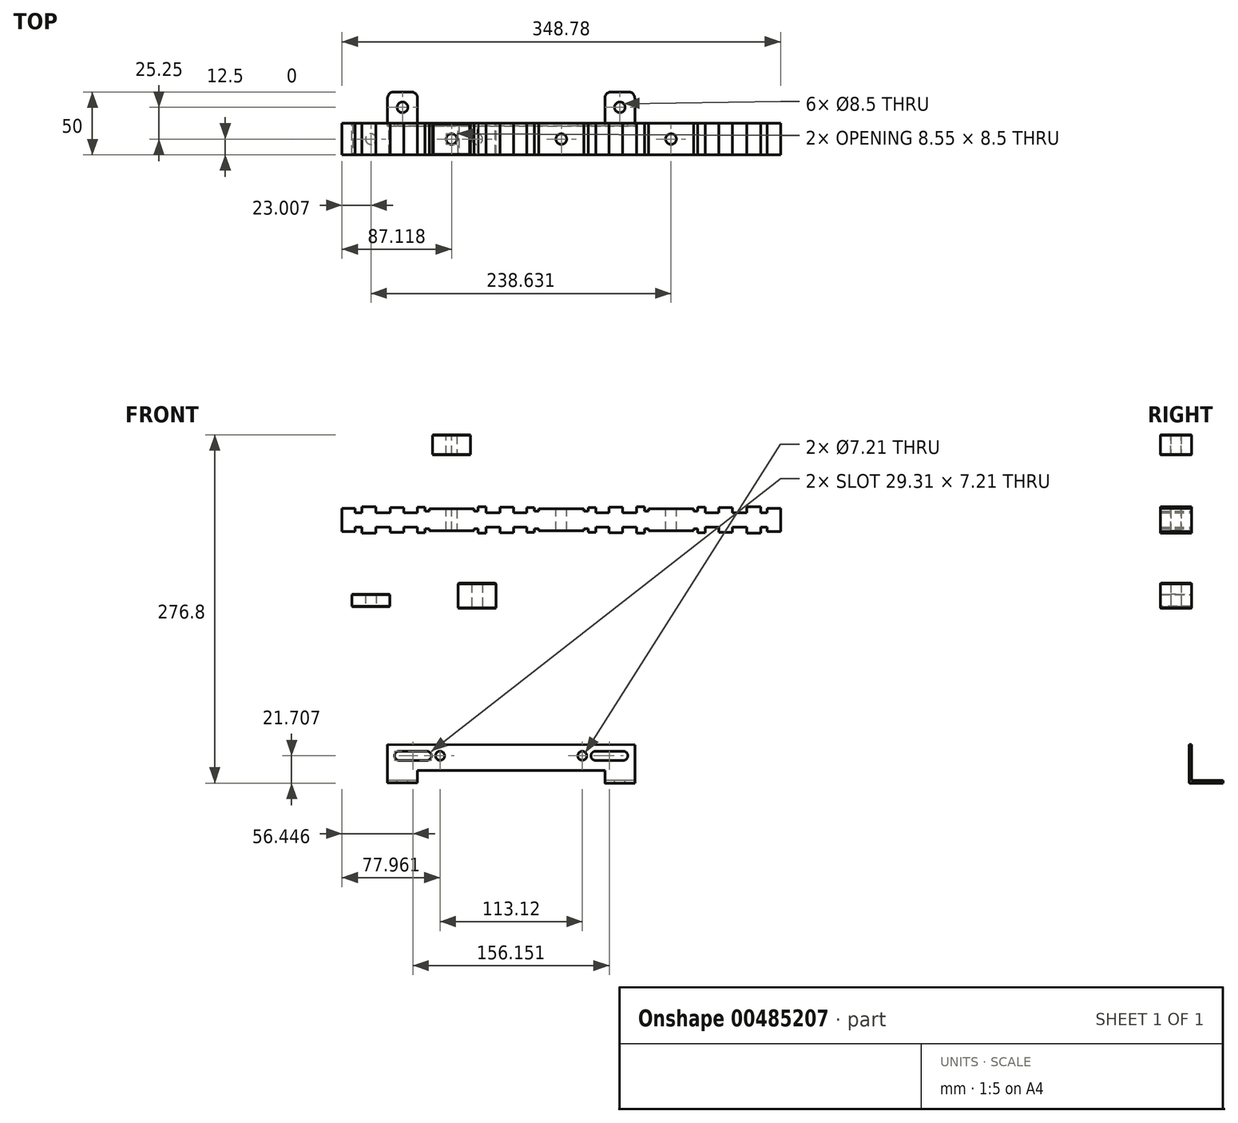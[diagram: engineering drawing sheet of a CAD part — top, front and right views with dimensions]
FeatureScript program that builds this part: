
annotation { "Feature Type Name" : "Feature", "Feature Type Description" : "" }
export const myFeature = defineFeature(function(context is Context, id is Id, definition is map)
    precondition{}
    {
        {
            var Q0;
            Q0=qCreatedBy(makeId("Front.planeOp"),FACE);
            var sketch = newSketch(context, id + "F0", { "sketchPlane" : qUnion([Q0])});
            skLineSegment(sketch, "E0", {"start": v(-156.91, 5.74) * mm, "end": v(-156.91, -3.35) * mm});
            skLineSegment(sketch, "E1", {"start": v(-156.91, -3.35) * mm, "end": v(-146.35, -3.35) * mm});
            skLineSegment(sketch, "E2", {"start": v(-146.35, -3.35) * mm, "end": v(-146.35, 0) * mm});
            skLineSegment(sketch, "E3", {"start": v(-146.35, 0) * mm, "end": v(-141.22, 0) * mm});
            skLineSegment(sketch, "E4", {"start": v(-141.22, 0) * mm, "end": v(-141.22, -4.82) * mm});
            skLineSegment(sketch, "E5", {"start": v(-141.22, -4.82) * mm, "end": v(-129.92, -4.82) * mm});
            skLineSegment(sketch, "E6", {"start": v(-129.92, -4.82) * mm, "end": v(-129.92, 0) * mm});
            skLineSegment(sketch, "E7", {"start": v(-129.92, 0) * mm, "end": v(-118.63, 0) * mm});
            skLineSegment(sketch, "E8", {"start": v(-118.63, 0) * mm, "end": v(-118.63, -4.17) * mm});
            skLineSegment(sketch, "E9", {"start": v(-118.63, -4.17) * mm, "end": v(-107.86, -4.17) * mm});
            skLineSegment(sketch, "E10", {"start": v(-107.86, -4.17) * mm, "end": v(-107.86, 0) * mm});
            skLineSegment(sketch, "E11", {"start": v(-107.86, 0) * mm, "end": v(-96.96, 0) * mm});
            skLineSegment(sketch, "E12", {"start": v(-96.96, 0) * mm, "end": v(-96.96, -4.43) * mm});
            skLineSegment(sketch, "E13", {"start": v(-96.96, -4.43) * mm, "end": v(-90.86, -4.43) * mm});
            skLineSegment(sketch, "E14", {"start": v(-90.86, -4.43) * mm, "end": v(-90.86, -1.18) * mm});
            skLineSegment(sketch, "E15", {"start": v(-90.86, -1.18) * mm, "end": v(-87.61, -1.18) * mm});
            skLineSegment(sketch, "E16", {"start": v(-87.61, -1.18) * mm, "end": v(-87.61, -3) * mm});
            skLineSegment(sketch, "E17", {"start": v(-87.61, -3) * mm, "end": v(-51.92, -3) * mm});
            skLineSegment(sketch, "E18", {"start": v(-51.92, -3) * mm, "end": v(-51.92, -1.18) * mm});
            skPoint(sketch, "E18.endSnap0", {"position": v(-89.24, -1.18) * mm});
            skLineSegment(sketch, "E19", {"start": v(-51.92, -1.18) * mm, "end": v(-48.79, -1.18) * mm});
            skLineSegment(sketch, "E20", {"start": v(-48.79, -1.18) * mm, "end": v(-48.79, -4.73) * mm});
            skLineSegment(sketch, "E21", {"start": v(-48.79, -4.73) * mm, "end": v(-42.49, -4.73) * mm});
            skLineSegment(sketch, "E22", {"start": v(-42.49, -4.73) * mm, "end": v(-42.49, 0) * mm});
            skLineSegment(sketch, "E23", {"start": v(-42.49, 0) * mm, "end": v(-31.4, 0) * mm});
            skLineSegment(sketch, "E24", {"start": v(-31.4, 0) * mm, "end": v(-31.4, -4.37) * mm});
            skLineSegment(sketch, "E25", {"start": v(-31.4, -4.37) * mm, "end": v(-20.51, -4.37) * mm});
            skLineSegment(sketch, "E26", {"start": v(-20.51, -4.37) * mm, "end": v(-20.51, 0) * mm});
            skLineSegment(sketch, "E27", {"start": v(-20.51, 0) * mm, "end": v(-9.94, 0) * mm});
            skLineSegment(sketch, "E28", {"start": v(-9.94, 0) * mm, "end": v(-9.94, -4.17) * mm});
            skLineSegment(sketch, "E29", {"start": v(-9.94, -4.17) * mm, "end": v(-4.1, -4.17) * mm});
            skLineSegment(sketch, "E30", {"start": v(-4.1, -4.17) * mm, "end": v(-4.1, -1.18) * mm});
            skLineSegment(sketch, "E31", {"start": v(-4.1, -1.18) * mm, "end": v(-0.58, -1.18) * mm});
            skLineSegment(sketch, "E32", {"start": v(-0.58, -1.18) * mm, "end": v(-0.58, -3) * mm});
            skLineSegment(sketch, "E33", {"start": v(-0.58, -3) * mm, "end": v(17.48, -3) * mm});
            skLineSegment(sketch, "E34.MirrorCS", {"start": v(-4.1, 15.64) * mm, "end": v(-4.1, 12.65) * mm});
            skLineSegment(sketch, "E35.MirrorCS", {"start": v(-90.86, 15.9) * mm, "end": v(-90.86, 12.65) * mm});
            skLineSegment(sketch, "E36.MirrorCS", {"start": v(-90.86, 12.65) * mm, "end": v(-87.61, 12.65) * mm});
            skLineSegment(sketch, "E37.MirrorCS", {"start": v(-4.1, 12.65) * mm, "end": v(-0.58, 12.65) * mm});
            skLineSegment(sketch, "E38.MirrorCS", {"start": v(-96.96, 11.47) * mm, "end": v(-96.96, 15.9) * mm});
            skLineSegment(sketch, "E39.MirrorCS", {"start": v(-9.94, 15.64) * mm, "end": v(-4.1, 15.64) * mm});
            skLineSegment(sketch, "E40.MirrorCS", {"start": v(-96.96, 15.9) * mm, "end": v(-90.86, 15.9) * mm});
            skLineSegment(sketch, "E41.MirrorCS", {"start": v(-87.61, 12.65) * mm, "end": v(-87.61, 14.47) * mm});
            skLineSegment(sketch, "E42.MirrorCS", {"start": v(-0.58, 12.65) * mm, "end": v(-0.58, 14.47) * mm});
            skLineSegment(sketch, "E43.MirrorCS", {"start": v(-20.51, 15.84) * mm, "end": v(-20.51, 11.47) * mm});
            skLineSegment(sketch, "E44.MirrorCS", {"start": v(-107.86, 15.64) * mm, "end": v(-107.86, 11.47) * mm});
            skLineSegment(sketch, "E45.MirrorCS", {"start": v(-146.35, 11.47) * mm, "end": v(-141.22, 11.47) * mm});
            skLineSegment(sketch, "E46.MirrorCS", {"start": v(-156.91, 14.82) * mm, "end": v(-146.35, 14.82) * mm});
            skLineSegment(sketch, "E47.MirrorCS", {"start": v(-146.35, 14.82) * mm, "end": v(-146.35, 11.47) * mm});
            skLineSegment(sketch, "E48.MirrorCS", {"start": v(-141.22, 11.47) * mm, "end": v(-141.22, 16.29) * mm});
            skLineSegment(sketch, "E49.MirrorCS", {"start": v(-156.91, 5.74) * mm, "end": v(-156.91, 14.82) * mm});
            skLineSegment(sketch, "E50.MirrorCS", {"start": v(-51.92, 12.65) * mm, "end": v(-48.79, 12.65) * mm});
            skLineSegment(sketch, "E51.MirrorCS", {"start": v(-42.49, 11.47) * mm, "end": v(-31.4, 11.47) * mm});
            skLineSegment(sketch, "E52.MirrorCS", {"start": v(-51.92, 14.47) * mm, "end": v(-51.92, 12.65) * mm});
            skLineSegment(sketch, "E53.MirrorCS", {"start": v(-9.94, 11.47) * mm, "end": v(-9.94, 15.64) * mm});
            skLineSegment(sketch, "E54.MirrorCS", {"start": v(-48.79, 16.2) * mm, "end": v(-42.49, 16.2) * mm});
            skLineSegment(sketch, "E55.MirrorCS", {"start": v(-107.86, 11.47) * mm, "end": v(-96.96, 11.47) * mm});
            skLineSegment(sketch, "E56.MirrorCS", {"start": v(-118.63, 11.47) * mm, "end": v(-118.63, 15.64) * mm});
            skLineSegment(sketch, "E57.MirrorCS", {"start": v(-31.4, 11.47) * mm, "end": v(-31.4, 15.84) * mm});
            skLineSegment(sketch, "E58.MirrorCS", {"start": v(-31.4, 15.84) * mm, "end": v(-20.51, 15.84) * mm});
            skLineSegment(sketch, "E59.MirrorCS", {"start": v(-129.92, 16.29) * mm, "end": v(-129.92, 11.47) * mm});
            skLineSegment(sketch, "E60.MirrorCS", {"start": v(-129.92, 11.47) * mm, "end": v(-118.63, 11.47) * mm});
            skLineSegment(sketch, "E61.MirrorCS", {"start": v(-118.63, 15.64) * mm, "end": v(-107.86, 15.64) * mm});
            skLineSegment(sketch, "E62.MirrorCS", {"start": v(-42.49, 16.2) * mm, "end": v(-42.49, 11.47) * mm});
            skLineSegment(sketch, "E63.MirrorCS", {"start": v(-20.51, 11.47) * mm, "end": v(-9.94, 11.47) * mm});
            skLineSegment(sketch, "E64.MirrorCS", {"start": v(-48.79, 12.65) * mm, "end": v(-48.79, 16.2) * mm});
            skLineSegment(sketch, "E65.MirrorCS", {"start": v(-141.22, 16.29) * mm, "end": v(-129.92, 16.29) * mm});
            skLineSegment(sketch, "E66.MirrorCS", {"start": v(-87.61, 14.47) * mm, "end": v(-51.92, 14.47) * mm});
            skLineSegment(sketch, "E67.MirrorCS", {"start": v(-0.58, 14.47) * mm, "end": v(17.48, 14.47) * mm});
            skLineSegment(sketch, "E68.MirrorCS", {"start": v(-84.53, -3.04) * mm, "end": v(-54.8, -3.04) * mm});
            skPoint(sketch, "E69.MirrorP", {"position": v(-89.24, 12.65) * mm});
            skLineSegment(sketch, "E70.MirrorCS", {"start": v(39.06, -1.18) * mm, "end": v(35.54, -1.18) * mm});
            skLineSegment(sketch, "E71.MirrorCS", {"start": v(35.54, -1.18) * mm, "end": v(35.54, -3) * mm});
            skLineSegment(sketch, "E72.MirrorCS", {"start": v(39.06, -4.17) * mm, "end": v(39.06, -1.18) * mm});
            skLineSegment(sketch, "E73.MirrorCS", {"start": v(125.82, -1.18) * mm, "end": v(122.57, -1.18) * mm});
            skLineSegment(sketch, "E74.MirrorCS", {"start": v(125.82, 12.65) * mm, "end": v(122.57, 12.65) * mm});
            skLineSegment(sketch, "E75.MirrorCS", {"start": v(122.57, -1.18) * mm, "end": v(122.57, -3) * mm});
            skLineSegment(sketch, "E76.MirrorCS", {"start": v(83.75, -1.18) * mm, "end": v(83.75, -4.73) * mm});
            skLineSegment(sketch, "E77.MirrorCS", {"start": v(125.82, 15.9) * mm, "end": v(125.82, 12.65) * mm});
            skLineSegment(sketch, "E78.MirrorCS", {"start": v(125.82, -4.43) * mm, "end": v(125.82, -1.18) * mm});
            skLineSegment(sketch, "E79.MirrorCS", {"start": v(86.88, 12.65) * mm, "end": v(83.75, 12.65) * mm});
            skLineSegment(sketch, "E80.MirrorCS", {"start": v(122.57, 12.65) * mm, "end": v(122.57, 14.47) * mm});
            skLineSegment(sketch, "E81.MirrorCS", {"start": v(86.88, -1.18) * mm, "end": v(83.75, -1.18) * mm});
            skLineSegment(sketch, "E82.MirrorCS", {"start": v(86.88, -3) * mm, "end": v(86.88, -1.18) * mm});
            skLineSegment(sketch, "E83.MirrorCS", {"start": v(142.82, 0) * mm, "end": v(131.92, 0) * mm});
            skLineSegment(sketch, "E84.MirrorCS", {"start": v(35.54, 12.65) * mm, "end": v(35.54, 14.47) * mm});
            skLineSegment(sketch, "E85.MirrorCS", {"start": v(55.47, 0) * mm, "end": v(44.9, 0) * mm});
            skLineSegment(sketch, "E86.MirrorCS", {"start": v(164.88, -4.82) * mm, "end": v(164.88, 0) * mm});
            skLineSegment(sketch, "E87.MirrorCS", {"start": v(39.06, 15.64) * mm, "end": v(39.06, 12.65) * mm});
            skLineSegment(sketch, "E88.MirrorCS", {"start": v(77.45, 16.2) * mm, "end": v(77.45, 11.47) * mm});
            skLineSegment(sketch, "E89.MirrorCS", {"start": v(86.88, 14.47) * mm, "end": v(86.88, 12.65) * mm});
            skLineSegment(sketch, "E90.MirrorCS", {"start": v(55.47, 15.84) * mm, "end": v(55.47, 11.47) * mm});
            skLineSegment(sketch, "E91.MirrorCS", {"start": v(83.75, -4.73) * mm, "end": v(77.45, -4.73) * mm});
            skLineSegment(sketch, "E92.MirrorCS", {"start": v(44.9, 0) * mm, "end": v(44.9, -4.17) * mm});
            skLineSegment(sketch, "E93.MirrorCS", {"start": v(153.6, 0) * mm, "end": v(153.6, -4.17) * mm});
            skLineSegment(sketch, "E94.MirrorCS", {"start": v(77.45, 11.47) * mm, "end": v(66.35, 11.47) * mm});
            skLineSegment(sketch, "E95.MirrorCS", {"start": v(181.3, 14.82) * mm, "end": v(181.3, 11.47) * mm});
            skLineSegment(sketch, "E96.MirrorCS", {"start": v(131.92, -4.43) * mm, "end": v(125.82, -4.43) * mm});
            skLineSegment(sketch, "E97.MirrorCS", {"start": v(55.47, 11.47) * mm, "end": v(44.9, 11.47) * mm});
            skLineSegment(sketch, "E98.MirrorCS", {"start": v(44.9, 11.47) * mm, "end": v(44.9, 15.64) * mm});
            skLineSegment(sketch, "E99.MirrorCS", {"start": v(164.88, 11.47) * mm, "end": v(153.6, 11.47) * mm});
            skLineSegment(sketch, "E100.MirrorCS", {"start": v(77.45, -4.73) * mm, "end": v(77.45, 0) * mm});
            skLineSegment(sketch, "E101.MirrorCS", {"start": v(142.82, 15.64) * mm, "end": v(142.82, 11.47) * mm});
            skLineSegment(sketch, "E102.MirrorCS", {"start": v(39.06, 12.65) * mm, "end": v(35.54, 12.65) * mm});
            skLineSegment(sketch, "E103.MirrorCS", {"start": v(44.9, -4.17) * mm, "end": v(39.06, -4.17) * mm});
            skLineSegment(sketch, "E104.MirrorCS", {"start": v(153.6, 11.47) * mm, "end": v(153.6, 15.64) * mm});
            skLineSegment(sketch, "E105.MirrorCS", {"start": v(131.92, 15.9) * mm, "end": v(125.82, 15.9) * mm});
            skLineSegment(sketch, "E106.MirrorCS", {"start": v(131.92, 0) * mm, "end": v(131.92, -4.43) * mm});
            skLineSegment(sketch, "E107.MirrorCS", {"start": v(66.35, 0) * mm, "end": v(66.35, -4.37) * mm});
            skLineSegment(sketch, "E108.MirrorCS", {"start": v(44.9, 15.64) * mm, "end": v(39.06, 15.64) * mm});
            skLineSegment(sketch, "E109.MirrorCS", {"start": v(164.88, 0) * mm, "end": v(153.6, 0) * mm});
            skLineSegment(sketch, "E110.MirrorCS", {"start": v(164.88, 16.29) * mm, "end": v(164.88, 11.47) * mm});
            skLineSegment(sketch, "E111.MirrorCS", {"start": v(191.87, 5.74) * mm, "end": v(191.87, 14.82) * mm});
            skLineSegment(sketch, "E112.MirrorCS", {"start": v(176.17, 0) * mm, "end": v(176.17, -4.82) * mm});
            skLineSegment(sketch, "E113.MirrorCS", {"start": v(142.82, 11.47) * mm, "end": v(131.92, 11.47) * mm});
            skLineSegment(sketch, "E114.MirrorCS", {"start": v(55.47, -4.37) * mm, "end": v(55.47, 0) * mm});
            skLineSegment(sketch, "E115.MirrorCS", {"start": v(131.92, 11.47) * mm, "end": v(131.92, 15.9) * mm});
            skLineSegment(sketch, "E116.MirrorCS", {"start": v(66.35, 11.47) * mm, "end": v(66.35, 15.84) * mm});
            skLineSegment(sketch, "E117.MirrorCS", {"start": v(181.3, 0) * mm, "end": v(176.17, 0) * mm});
            skLineSegment(sketch, "E118.MirrorCS", {"start": v(142.82, -4.17) * mm, "end": v(142.82, 0) * mm});
            skLineSegment(sketch, "E119.MirrorCS", {"start": v(181.3, -3.35) * mm, "end": v(181.3, 0) * mm});
            skLineSegment(sketch, "E120.MirrorCS", {"start": v(181.3, 11.47) * mm, "end": v(176.17, 11.47) * mm});
            skLineSegment(sketch, "E121.MirrorCS", {"start": v(191.87, 5.74) * mm, "end": v(191.87, -3.35) * mm});
            skLineSegment(sketch, "E122.MirrorCS", {"start": v(176.17, 11.47) * mm, "end": v(176.17, 16.29) * mm});
            skLineSegment(sketch, "E123.MirrorCS", {"start": v(83.75, 16.2) * mm, "end": v(77.45, 16.2) * mm});
            skLineSegment(sketch, "E124.MirrorCS", {"start": v(77.45, 0) * mm, "end": v(66.35, 0) * mm});
            skLineSegment(sketch, "E125.MirrorCS", {"start": v(83.75, 12.65) * mm, "end": v(83.75, 16.2) * mm});
            skLineSegment(sketch, "E126.MirrorCS", {"start": v(119.49, -3.04) * mm, "end": v(89.76, -3.04) * mm});
            skLineSegment(sketch, "E127.MirrorCS", {"start": v(122.57, 14.47) * mm, "end": v(86.88, 14.47) * mm});
            skLineSegment(sketch, "E128.MirrorCS", {"start": v(176.17, 16.29) * mm, "end": v(164.88, 16.29) * mm});
            skLineSegment(sketch, "E129.MirrorCS", {"start": v(66.35, 15.84) * mm, "end": v(55.47, 15.84) * mm});
            skPoint(sketch, "E130.MirrorP", {"position": v(124.2, 12.65) * mm});
            skLineSegment(sketch, "E131.MirrorCS", {"start": v(119.49, 14.51) * mm, "end": v(89.76, 14.51) * mm});
            skPoint(sketch, "E132.MirrorP", {"position": v(124.2, -1.18) * mm});
            skLineSegment(sketch, "E133.MirrorCS", {"start": v(153.6, -4.17) * mm, "end": v(142.82, -4.17) * mm});
            skLineSegment(sketch, "E134.MirrorCS", {"start": v(35.54, 14.47) * mm, "end": v(17.48, 14.47) * mm});
            skLineSegment(sketch, "E135.MirrorCS", {"start": v(66.35, -4.37) * mm, "end": v(55.47, -4.37) * mm});
            skLineSegment(sketch, "E136.MirrorCS", {"start": v(176.17, -4.82) * mm, "end": v(164.88, -4.82) * mm});
            skLineSegment(sketch, "E137.MirrorCS", {"start": v(153.6, 15.64) * mm, "end": v(142.82, 15.64) * mm});
            skLineSegment(sketch, "E138.MirrorCS", {"start": v(35.54, -3) * mm, "end": v(17.48, -3) * mm});
            skLineSegment(sketch, "E139.MirrorCS", {"start": v(191.87, 14.82) * mm, "end": v(181.3, 14.82) * mm});
            skLineSegment(sketch, "E140.MirrorCS", {"start": v(122.57, -3) * mm, "end": v(86.88, -3) * mm});
            skLineSegment(sketch, "E141.MirrorCS", {"start": v(191.87, -3.35) * mm, "end": v(181.3, -3.35) * mm});
            skSolve(sketch);
        }
        {
            var Q0;
            Q0=makeQuery(id+"F0.imprint","IMPRINT",FACE,{"disambiguationData":[TD([[makeQuery(id+"F0.imprint","IMPRINT",EDGE,{"derivedFrom":sQuery(id+"F0.wireOp",EDGE,"E0")}),1.0]])]});
            extrude(context, id + "F1", {"entities" : qUnion([Q0]), "depth" : 25 * mm});
        }
        {
            var Q0;
            Q0=qCreatedBy(makeId("Front.planeOp"),FACE);
            var sketch = newSketch(context, id + "F2", { "sketchPlane" : qUnion([Q0])});
            skLineSegment(sketch, "E142.bottom", {"start": v(-64.44, -44.48) * mm, "end": v(-34.44, -44.48) * mm});
            skLineSegment(sketch, "E142.top", {"start": v(-64.44, -64.48) * mm, "end": v(-34.44, -64.48) * mm});
            skLineSegment(sketch, "E142.left", {"start": v(-64.44, -44.48) * mm, "end": v(-64.44, -64.48) * mm});
            skLineSegment(sketch, "E142.right", {"start": v(-34.44, -44.48) * mm, "end": v(-34.44, -64.48) * mm});
            skSolve(sketch);
        }
        {
            var Q0;
            Q0=makeQuery(id+"F2.imprint","IMPRINT",FACE,{"disambiguationData":[TD([[makeQuery(id+"F2.imprint","IMPRINT",EDGE,{"derivedFrom":sQuery(id+"F2.wireOp",EDGE,"E142.bottom")}),-1.0]])]});
            extrude(context, id + "F3", {"entities" : qUnion([Q0]), "depth" : 25 * mm});
        }
        {
            var Q0;
            Q0=qCreatedBy(makeId("Front.planeOp"),FACE);
            var sketch = newSketch(context, id + "F4", { "sketchPlane" : qUnion([Q0])});
            skLineSegment(sketch, "E143.bottom", {"start": v(-84.82, 73.4) * mm, "end": v(-54.82, 73.4) * mm});
            skLineSegment(sketch, "E143.top", {"start": v(-84.82, 57.4) * mm, "end": v(-54.82, 57.4) * mm});
            skLineSegment(sketch, "E143.left", {"start": v(-84.82, 73.4) * mm, "end": v(-84.82, 57.4) * mm});
            skLineSegment(sketch, "E143.right", {"start": v(-54.82, 73.4) * mm, "end": v(-54.82, 57.4) * mm});
            skSolve(sketch);
        }
        {
            var Q0;
            Q0=makeQuery(id+"F4.imprint","IMPRINT",FACE,{"disambiguationData":[TD([[makeQuery(id+"F4.imprint","IMPRINT",EDGE,{"derivedFrom":sQuery(id+"F4.wireOp",EDGE,"E143.bottom")}),-1.0]])]});
            extrude(context, id + "F5", {"entities" : qUnion([Q0]), "depth" : 25 * mm});
        }
        {
            var Q0;
            Q0=qCreatedBy(makeId("Front.planeOp"),FACE);
            var sketch = newSketch(context, id + "F6", { "sketchPlane" : qUnion([Q0])});
            skLineSegment(sketch, "E144.bottom", {"start": v(-148.9, -53.25) * mm, "end": v(-118.9, -53.25) * mm});
            skLineSegment(sketch, "E144.top", {"start": v(-148.9, -63.25) * mm, "end": v(-118.9, -63.25) * mm});
            skLineSegment(sketch, "E144.left", {"start": v(-148.9, -53.25) * mm, "end": v(-148.9, -63.25) * mm});
            skLineSegment(sketch, "E144.right", {"start": v(-118.9, -53.25) * mm, "end": v(-118.9, -63.25) * mm});
            skSolve(sketch);
        }
        {
            var Q0;
            Q0=makeQuery(id+"F6.imprint","IMPRINT",FACE,{"disambiguationData":[TD([[makeQuery(id+"F6.imprint","IMPRINT",EDGE,{"derivedFrom":sQuery(id+"F6.wireOp",EDGE,"E144.bottom")}),-1.0]])]});
            extrude(context, id + "F7", {"entities" : qUnion([Q0]), "depth" : 25 * mm});
        }
        {
            var Q0;
            Q0=makeQuery(id+"F3.opExtrude","CAP_EDGE",EDGE,{"disambiguationData":[OSD([sQuery(id+"F2.wireOp",EDGE,"E142.bottom")])],"isStart":false});
            var Q1;
            Q1=makeQuery(id+"F3.opExtrude","SWEPT_FACE",FACE,{"disambiguationData":[OSD([sQuery(id+"F2.wireOp",EDGE,"E142.bottom")])]});
            var Q2;
            Q2=makeQuery(id+"F3.opExtrude","SWEPT_FACE",FACE,{"disambiguationData":[OSD([sQuery(id+"F2.wireOp",EDGE,"E142.top")])]});
            var Q3;
            Q3=makeQuery(id+"F7.opExtrude","SWEPT_FACE",FACE,{"disambiguationData":[OSD([sQuery(id+"F6.wireOp",EDGE,"E144.bottom")])]});
            var Q4;
            Q4=makeQuery(id+"F7.opExtrude","SWEPT_FACE",FACE,{"disambiguationData":[OSD([sQuery(id+"F6.wireOp",EDGE,"E144.top")])]});
            var Q5;
            Q5=makeQuery(id+"F5.opExtrude","SWEPT_FACE",FACE,{"disambiguationData":[OSD([sQuery(id+"F4.wireOp",EDGE,"E143.bottom")])]});
            var Q6;
            Q6=makeQuery(id+"F5.opExtrude","SWEPT_FACE",FACE,{"disambiguationData":[OSD([sQuery(id+"F4.wireOp",EDGE,"E143.top")])]});
            chamfer(context, id + "F8", {"entities" : qUnion([Q0, Q1, Q2, Q3, Q4, Q5, Q6]), "width" : 0.5 * mm, "tangentPropagation" : true});
        }
        {
            var Q0;
            Q0=qCreatedBy(makeId("Front.planeOp"),FACE);
            var sketch = newSketch(context, id + "F9", { "sketchPlane" : qUnion([Q0])});
            skLineSegment(sketch, "E145", {"start": v(-94, -213.92) * mm, "end": v(-94, -233.92) * mm});
            skLineSegment(sketch, "E146", {"start": v(-120.67, -172.6) * mm, "end": v(-120.67, -203.16) * mm});
            skLineSegment(sketch, "E147", {"start": v(-120.67, -203.16) * mm, "end": v(-96.89, -203.16) * mm});
            skLineSegment(sketch, "E148", {"start": v(-96.89, -203.16) * mm, "end": v(-96.89, -193.38) * mm});
            skLineSegment(sketch, "E149", {"start": v(-96.89, -193.38) * mm, "end": v(52.1, -193.38) * mm});
            skLineSegment(sketch, "E150", {"start": v(52.1, -193.38) * mm, "end": v(52.1, -203.4) * mm});
            skLineSegment(sketch, "E151", {"start": v(52.1, -203.4) * mm, "end": v(75.9, -203.4) * mm});
            skLineSegment(sketch, "E152", {"start": v(75.9, -203.4) * mm, "end": v(75.9, -172.9) * mm});
            skLineSegment(sketch, "E153", {"start": v(75.9, -172.9) * mm, "end": v(-120.67, -172.6) * mm});
            skCircle(sketch, "E154", {"center": v(-78.95, -181.7) * mm, "radius": 3.6 * mm});
            skArc(sketch, "E155", {"start": v(-90.01, -185.3) * mm, "mid": v(-85.81, -182.02) * mm, "end": v(-89.43, -178.1) * mm});
            skLineSegment(sketch, "E156", {"start": v(-112.3, -178.1) * mm, "end": v(-89.43, -178.1) * mm});
            skLineSegment(sketch, "E157.MirrorCS", {"start": v(-112.3, -185.3) * mm, "end": v(-90.01, -185.3) * mm});
            skArc(sketch, "E158.MirrorC", {"start": v(-112.3, -185.3) * mm, "mid": v(-115.12, -181.7) * mm, "end": v(-112.3, -178.1) * mm});
            skLineSegment(sketch, "E159", {"start": v(-22.39, -172.76) * mm, "end": v(-22.39, -193.38) * mm});
            skCircle(sketch, "E160.MirrorC", {"center": v(34.17, -181.7) * mm, "radius": 3.6 * mm});
            skArc(sketch, "E161.MirrorCS", {"start": v(45.23, -185.3) * mm, "mid": v(41.03, -182.02) * mm, "end": v(44.65, -178.1) * mm});
            skLineSegment(sketch, "E162.MirrorCS", {"start": v(67.52, -178.1) * mm, "end": v(44.65, -178.1) * mm});
            skLineSegment(sketch, "E163.MirrorCS", {"start": v(67.52, -185.3) * mm, "end": v(45.23, -185.3) * mm});
            skArc(sketch, "E164.MirrorCS", {"start": v(67.52, -185.3) * mm, "mid": v(70.34, -181.7) * mm, "end": v(67.52, -178.1) * mm});
            skSolve(sketch);
        }
        {
            var Q0;
            Q0 = qSketchRegion(id + "F9", true);
            extrude(context, id + "F10", {"entities" : qUnion([Q0]), "depth" : 2 * mm});
        }
        {
            var Q0;
            Q0=makeQuery(id+"F10.opExtrude","CAP_FACE",FACE,{"disambiguationData":[OSD([sQuery(id+"F9.wireOp",EDGE,"E146"),sQuery(id+"F9.wireOp",EDGE,"E147"),sQuery(id+"F9.wireOp",EDGE,"E148"),sQuery(id+"F9.wireOp",EDGE,"E149"),sQuery(id+"F9.wireOp",EDGE,"E150"),sQuery(id+"F9.wireOp",EDGE,"E151"),sQuery(id+"F9.wireOp",EDGE,"E152"),sQuery(id+"F9.wireOp",EDGE,"E153"),sQuery(id+"F9.wireOp",EDGE,"E154"),sQuery(id+"F9.wireOp",EDGE,"E155"),sQuery(id+"F9.wireOp",EDGE,"E156"),sQuery(id+"F9.wireOp",EDGE,"E157.MirrorCS"),sQuery(id+"F9.wireOp",EDGE,"E158.MirrorC"),sQuery(id+"F9.wireOp",EDGE,"E160.MirrorC"),sQuery(id+"F9.wireOp",EDGE,"E161.MirrorCS"),sQuery(id+"F9.wireOp",EDGE,"E162.MirrorCS"),sQuery(id+"F9.wireOp",EDGE,"E163.MirrorCS"),sQuery(id+"F9.wireOp",EDGE,"E164.MirrorCS")])],"isStart":true});
            var sketch = newSketch(context, id + "F11", { "sketchPlane" : qUnion([Q0])});
            skLineSegment(sketch, "E165", {"start": v(-75.9, -201.4) * mm, "end": v(-52.1, -201.4) * mm});
            skLineSegment(sketch, "E166.MirrorCS", {"start": v(120.7, -201.11) * mm, "end": v(96.91, -201.18) * mm});
            skLineSegment(sketch, "E167.top", {"start": v(-75.9, -203.4) * mm, "end": v(-52.1, -203.4) * mm});
            skLineSegment(sketch, "E167.left", {"start": v(-75.9, -201.4) * mm, "end": v(-75.9, -203.4) * mm});
            skLineSegment(sketch, "E167.right", {"start": v(-52.1, -201.4) * mm, "end": v(-52.1, -203.4) * mm});
            skLineSegment(sketch, "E168.bottom", {"start": v(96.91, -201.18) * mm, "end": v(120.67, -201.18) * mm});
            skLineSegment(sketch, "E168.top", {"start": v(96.91, -203.16) * mm, "end": v(120.67, -203.16) * mm});
            skLineSegment(sketch, "E168.left", {"start": v(96.91, -201.18) * mm, "end": v(96.91, -203.16) * mm});
            skLineSegment(sketch, "E168.right", {"start": v(120.67, -201.18) * mm, "end": v(120.67, -203.16) * mm});
            skSolve(sketch);
        }
        {
            var Q0;
            Q0=makeQuery(id+"F11.imprint","IMPRINT",FACE,{"disambiguationData":[TD([[makeQuery(id+"F11.imprint","IMPRINT",EDGE,{"derivedFrom":sQuery(id+"F11.wireOp",EDGE,"E165")}),-1.0]])]});
            var Q1;
            Q1=makeQuery(id+"F11.imprint","IMPRINT",FACE,{"disambiguationData":[TD([[makeQuery(id+"F11.imprint","IMPRINT",EDGE,{"derivedFrom":sQuery(id+"F11.wireOp",EDGE,"E168.bottom")}),-1.0]])]});
            extrude(context, id + "F12", {"entities" : qUnion([Q0, Q1]), "operationType" : NewBodyOperationType.ADD, "depth" : 25 * mm});
        }
        {
            var Q0;
            Q0=makeQuery(id+"F12.opExtrude","CAP_EDGE",EDGE,{"disambiguationData":[OSD([sQuery(id+"F11.wireOp",EDGE,"E165")])],"isStart":true});
            var Q1;
            Q1=makeQuery(id+"F12.opExtrude","CAP_EDGE",EDGE,{"disambiguationData":[OSD([sQuery(id+"F11.wireOp",EDGE,"E168.bottom")])],"isStart":true});
            var Q2;
            Q2=makeQuery(id+"F10.opExtrude","CAP_EDGE",EDGE,{"disambiguationData":[OSD([sQuery(id+"F9.wireOp",EDGE,"E151")])],"isStart":false});
            var Q3;
            Q3=makeQuery(id+"F10.opExtrude","CAP_EDGE",EDGE,{"disambiguationData":[OSD([sQuery(id+"F9.wireOp",EDGE,"E147")])],"isStart":false});
            fillet(context, id + "F13", {"entities" : qUnion([Q0, Q1, Q2, Q3]), "radius" : 0.5 * mm, "tangentPropagation" : true, "allowEdgeOverflow" : false});
        }
        {
            var Q0;
            Q0=makeQuery(id+"F12.opExtrude","CAP_EDGE",EDGE,{"disambiguationData":[OSD([sQuery(id+"F11.wireOp",EDGE,"E167.left")])],"isStart":false});
            var Q1;
            Q1=makeQuery(id+"F12.opExtrude","CAP_EDGE",EDGE,{"disambiguationData":[OSD([sQuery(id+"F11.wireOp",EDGE,"E167.right")])],"isStart":false});
            var Q2;
            Q2=makeQuery(id+"F12.opExtrude","CAP_EDGE",EDGE,{"disambiguationData":[OSD([sQuery(id+"F11.wireOp",EDGE,"E168.left")])],"isStart":false});
            var Q3;
            Q3=makeQuery(id+"F12.opExtrude","CAP_EDGE",EDGE,{"disambiguationData":[OSD([sQuery(id+"F11.wireOp",EDGE,"E168.right")])],"isStart":false});
            fillet(context, id + "F14", {"entities" : qUnion([Q0, Q1, Q2, Q3]), "radius" : 5 * mm, "tangentPropagation" : true, "allowEdgeOverflow" : false});
        }
        {
            var Q0;
            Q0=makeQuery(id+"F12.opExtrude","SWEPT_FACE",FACE,{"disambiguationData":[OSD([sQuery(id+"F11.wireOp",EDGE,"E165")])]});
            var sketch = newSketch(context, id + "F15", { "sketchPlane" : qUnion([Q0])});
            skCircle(sketch, "E169", {"center": v(64, 12.75) * mm, "radius": 4.25 * mm});
            skSolve(sketch);
        }
        {
            var Q0;
            Q0=makeQuery(id+"F12.opExtrude","SWEPT_FACE",FACE,{"disambiguationData":[OSD([sQuery(id+"F11.wireOp",EDGE,"E168.bottom")])]});
            var sketch = newSketch(context, id + "F16", { "sketchPlane" : qUnion([Q0])});
            skCircle(sketch, "E170", {"center": v(-108.8, 12.75) * mm, "radius": 4.25 * mm});
            skSolve(sketch);
        }
        {
            var Q0;
            Q0=makeQuery(id+"F15.imprint","IMPRINT",FACE,{"disambiguationData":[TD([[makeQuery(id+"F15.imprint","IMPRINT",EDGE,{"derivedFrom":sQuery(id+"F15.wireOp",EDGE,"E169")}),1.0]])]});
            var Q1;
            Q1=makeQuery(id+"F16.imprint","IMPRINT",FACE,{"disambiguationData":[TD([[makeQuery(id+"F16.imprint","IMPRINT",EDGE,{"derivedFrom":sQuery(id+"F16.wireOp",EDGE,"E170")}),1.0]])]});
            extrude(context, id + "F17", {"entities" : qUnion([Q0, Q1]), "operationType" : NewBodyOperationType.REMOVE, "endBound" : BoundingType.THROUGH_ALL, "oppositeDirection" : true, "depth" : 25 * mm});
        }
        {
            var Q0;
            Q0=makeQuery(id+"F1.opExtrude","SWEPT_FACE",FACE,{"disambiguationData":[OSD([sQuery(id+"F0.wireOp",EDGE,"E127.MirrorCS")])]});
            var sketch = newSketch(context, id + "F18", { "sketchPlane" : qUnion([Q0])});
            skCircle(sketch, "E171", {"center": v(104.73, -12.5) * mm, "radius": 4.25 * mm});
            skPoint(sketch, "E171.centerSnap0", {"position": v(122.57, -12.5) * mm});
            skPoint(sketch, "E171.centerSnap1", {"position": v(104.73, 0) * mm});
            skSolve(sketch);
        }
        {
            var Q0;
            Q0=makeQuery(id+"F1.opExtrude","SWEPT_FACE",FACE,{"disambiguationData":[OSD([sQuery(id+"F0.wireOp",EDGE,"E67.MirrorCS"),sQuery(id+"F0.wireOp",EDGE,"E134.MirrorCS")])]});
            var sketch = newSketch(context, id + "F19", { "sketchPlane" : qUnion([Q0])});
            skCircle(sketch, "E172", {"center": v(17.48, -12.5) * mm, "radius": 4.25 * mm});
            skPoint(sketch, "E172.centerSnap0", {"position": v(35.54, -12.5) * mm});
            skPoint(sketch, "E172.centerSnap1", {"position": v(17.48, 0) * mm});
            skSolve(sketch);
        }
        {
            var Q0;
            Q0=makeQuery(id+"F1.opExtrude","SWEPT_FACE",FACE,{"disambiguationData":[OSD([sQuery(id+"F0.wireOp",EDGE,"E17")])]});
            var sketch = newSketch(context, id + "F20", { "sketchPlane" : qUnion([Q0])});
            skCircle(sketch, "E173", {"center": v(-69.77, 12.5) * mm, "radius": 4.25 * mm});
            skPoint(sketch, "E173.centerSnap0", {"position": v(-51.92, 12.5) * mm});
            skPoint(sketch, "E173.centerSnap1", {"position": v(-69.77, 25) * mm});
            skSolve(sketch);
        }
        {
            var Q0;
            Q0=makeQuery(id+"F20.imprint","IMPRINT",FACE,{"disambiguationData":[TD([[makeQuery(id+"F20.imprint","IMPRINT",EDGE,{"derivedFrom":sQuery(id+"F20.wireOp",EDGE,"E173")}),1.0]])]});
            extrude(context, id + "F21", {"entities" : qUnion([Q0]), "operationType" : NewBodyOperationType.REMOVE, "endBound" : BoundingType.THROUGH_ALL, "oppositeDirection" : true, "depth" : 25 * mm});
        }
        {
            var Q0;
            Q0=makeQuery(id+"F19.imprint","IMPRINT",FACE,{"disambiguationData":[TD([[makeQuery(id+"F19.imprint","IMPRINT",EDGE,{"derivedFrom":sQuery(id+"F19.wireOp",EDGE,"E172")}),1.0]])]});
            var Q1;
            Q1=makeQuery(id+"F18.imprint","IMPRINT",FACE,{"disambiguationData":[TD([[makeQuery(id+"F18.imprint","IMPRINT",EDGE,{"derivedFrom":sQuery(id+"F18.wireOp",EDGE,"E171")}),1.0]])]});
            extrude(context, id + "F22", {"entities" : qUnion([Q0, Q1]), "operationType" : NewBodyOperationType.REMOVE, "endBound" : BoundingType.THROUGH_ALL, "oppositeDirection" : true, "depth" : 25 * mm});
        }
        {
            var Q0;
            Q0=makeQuery(id+"F5.opExtrude","SWEPT_FACE",FACE,{"disambiguationData":[OSD([sQuery(id+"F4.wireOp",EDGE,"E143.bottom")])]});
            var sketch = newSketch(context, id + "F23", { "sketchPlane" : qUnion([Q0])});
            skCircle(sketch, "E174", {"center": v(-69.82, -12.5) * mm, "radius": 4.25 * mm});
            skPoint(sketch, "E174.centerSnap0", {"position": v(-69.82, -24.5) * mm});
            skPoint(sketch, "E174.centerSnap1", {"position": v(-55.32, -12.5) * mm});
            skSolve(sketch);
        }
        {
            var Q0;
            Q0=makeQuery(id+"F23.imprint","IMPRINT",FACE,{"disambiguationData":[TD([[makeQuery(id+"F23.imprint","IMPRINT",EDGE,{"derivedFrom":sQuery(id+"F23.wireOp",EDGE,"E174")}),1.0]])]});
            extrude(context, id + "F24", {"entities" : qUnion([Q0]), "operationType" : NewBodyOperationType.REMOVE, "endBound" : BoundingType.THROUGH_ALL, "oppositeDirection" : true, "depth" : 25 * mm});
        }
        {
            var Q0;
            Q0=makeQuery(id+"F3.opExtrude","SWEPT_FACE",FACE,{"disambiguationData":[OSD([sQuery(id+"F2.wireOp",EDGE,"E142.top")])]});
            var sketch = newSketch(context, id + "F25", { "sketchPlane" : qUnion([Q0])});
            skCircle(sketch, "E175", {"center": v(-49.44, 12.5) * mm, "radius": 4.25 * mm});
            skPoint(sketch, "E175.centerSnap0", {"position": v(-34.94, 12.5) * mm});
            skPoint(sketch, "E175.centerSnap1", {"position": v(-49.44, 24.5) * mm});
            skSolve(sketch);
        }
        {
            var Q0;
            Q0=makeQuery(id+"F7.opExtrude","SWEPT_FACE",FACE,{"disambiguationData":[OSD([sQuery(id+"F6.wireOp",EDGE,"E144.top")])]});
            var sketch = newSketch(context, id + "F26", { "sketchPlane" : qUnion([Q0])});
            skCircle(sketch, "E176", {"center": v(-133.9, 12.5) * mm, "radius": 4.25 * mm});
            skPoint(sketch, "E176.centerSnap0", {"position": v(-133.9, 0.5) * mm});
            skPoint(sketch, "E176.centerSnap1", {"position": v(-119.4, 12.5) * mm});
            skSolve(sketch);
        }
        {
            var Q0;
            Q0=makeQuery(id+"F25.imprint","IMPRINT",FACE,{"disambiguationData":[TD([[makeQuery(id+"F25.imprint","IMPRINT",EDGE,{"derivedFrom":sQuery(id+"F25.wireOp",EDGE,"E175")}),1.0]])]});
            var Q1;
            Q1=sQuery(id+"F25.wireOp",EDGE,"E175");
            var Q2;
            Q2=makeQuery(id+"F3.opExtrude","SWEPT_FACE",FACE,{"disambiguationData":[OSD([sQuery(id+"F2.wireOp",EDGE,"E142.bottom")])]});
            extrude(context, id + "F27", {"entities" : qUnion([Q0]), "operationType" : NewBodyOperationType.REMOVE, "surfaceEntities" : qUnion([Q1]), "endBound" : BoundingType.UP_TO_SURFACE, "oppositeDirection" : true, "endBoundEntityFace" : qUnion([Q2]), "depth" : 25 * mm});
        }
        {
            var Q0;
            Q0=makeQuery(id+"F26.imprint","IMPRINT",FACE,{"disambiguationData":[TD([[makeQuery(id+"F26.imprint","IMPRINT",EDGE,{"derivedFrom":sQuery(id+"F26.wireOp",EDGE,"E176")}),1.0]])]});
            extrude(context, id + "F28", {"entities" : qUnion([Q0]), "operationType" : NewBodyOperationType.REMOVE, "oppositeDirection" : true, "depth" : 25 * mm});
        }
    });
